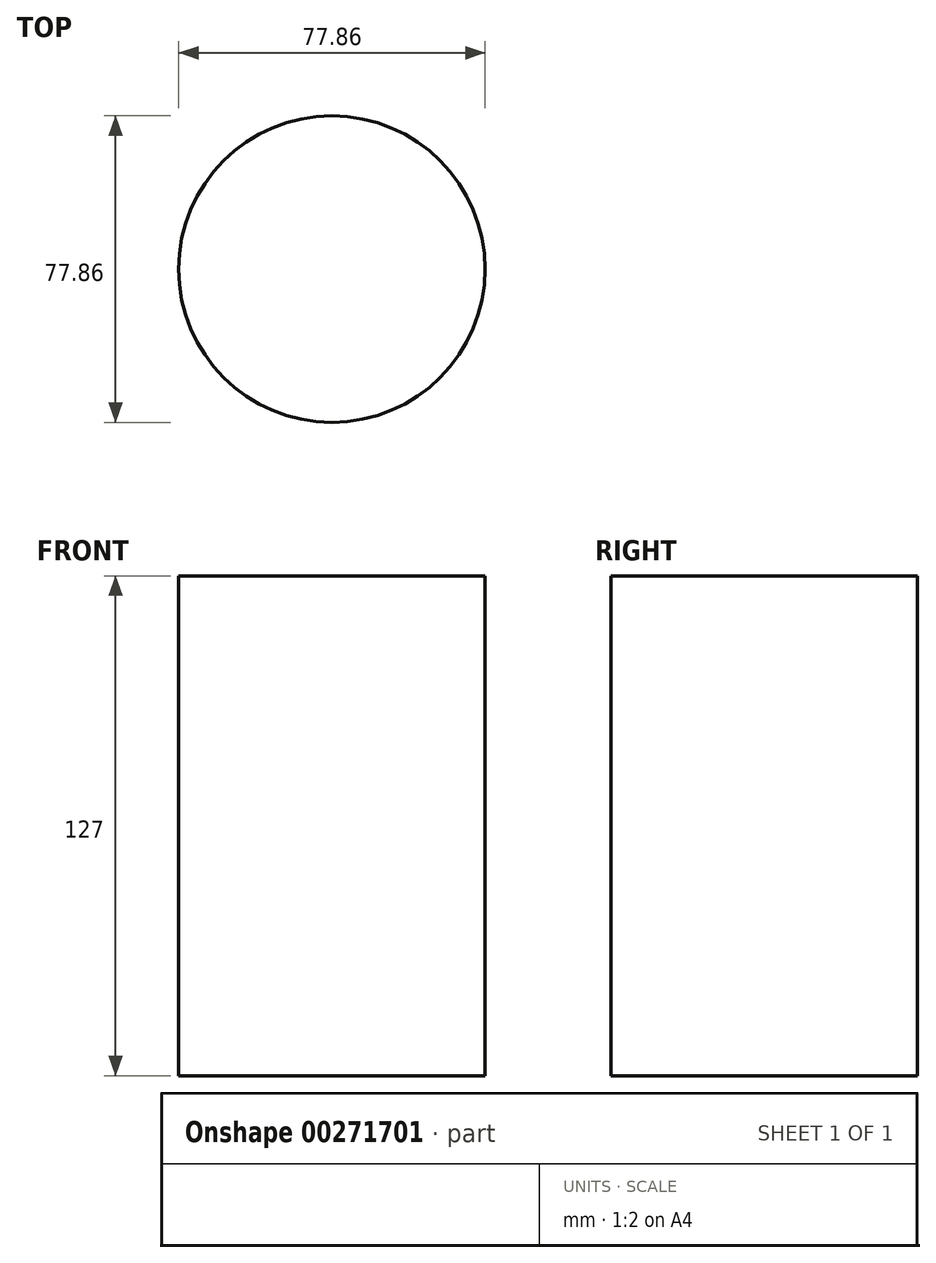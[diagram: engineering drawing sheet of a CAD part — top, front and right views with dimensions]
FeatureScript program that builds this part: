
annotation { "Feature Type Name" : "Feature", "Feature Type Description" : "" }
export const myFeature = defineFeature(function(context is Context, id is Id, definition is map)
    precondition{}
    {
        {
            var Q0;
            Q0=qCreatedBy(makeId("Top.planeOp"),FACE);
            var sketch = newSketch(context, id + "F0", { "sketchPlane" : qUnion([Q0])});
            skCircle(sketch, "E0", {"center": v(0, 0) * mm, "radius": 38.93 * mm});
            skSolve(sketch);
        }
        {
            var Q0;
            Q0=makeQuery(id+"F0.imprint","IMPRINT",FACE,{"disambiguationData":[TD([[makeQuery(id+"F0.imprint","IMPRINT",EDGE,{"derivedFrom":sQuery(id+"F0.wireOp",EDGE,"E0")}),1.0]])]});
            extrude(context, id + "F1", {"entities" : qUnion([Q0]), "depth" : 127 * mm});
        }
    });
